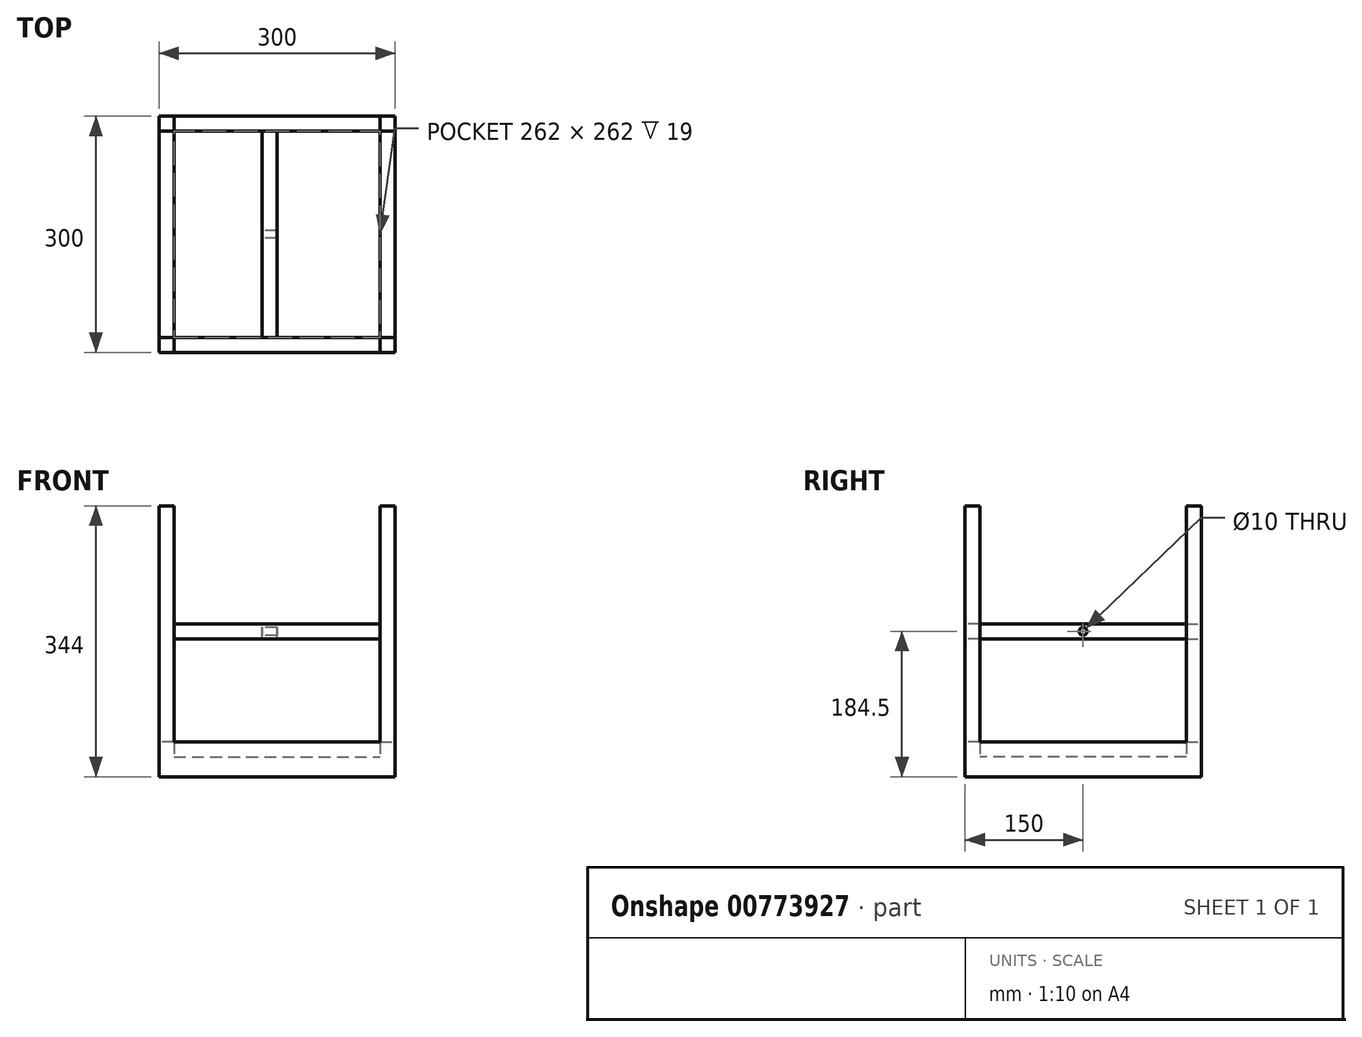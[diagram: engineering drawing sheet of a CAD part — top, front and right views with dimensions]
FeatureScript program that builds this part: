
annotation { "Feature Type Name" : "Feature", "Feature Type Description" : "" }
export const myFeature = defineFeature(function(context is Context, id is Id, definition is map)
    precondition{}
    {
        {
            var Q0;
            Q0=qCreatedBy(makeId("Top.planeOp"),FACE);
            var sketch = newSketch(context, id + "F0", { "sketchPlane" : qUnion([Q0])});
            skLineSegment(sketch, "E0.bottom", {"start": v(-150, -150) * mm, "end": v(150, -150) * mm});
            skLineSegment(sketch, "E0.top", {"start": v(-150, 150) * mm, "end": v(150, 150) * mm});
            skLineSegment(sketch, "E0.left", {"start": v(-150, -150) * mm, "end": v(-150, 150) * mm});
            skLineSegment(sketch, "E0.right", {"start": v(150, -150) * mm, "end": v(150, 150) * mm});
            skLineSegment(sketch, "E1.bottom", {"start": v(-131, 131) * mm, "end": v(131, 131) * mm});
            skLineSegment(sketch, "E1.top", {"start": v(-131, -131) * mm, "end": v(131, -131) * mm});
            skLineSegment(sketch, "E1.left", {"start": v(-131, 131) * mm, "end": v(-131, -131) * mm});
            skLineSegment(sketch, "E1.right", {"start": v(131, 131) * mm, "end": v(131, -131) * mm});
            skSolve(sketch);
        }
        {
            var Q0;
            Q0 = qSketchRegion(id + "F0", true);
            extrude(context, id + "F1", {"entities" : qUnion([Q0]), "depth" : 19 * mm, "offsetDistance" : 25 * mm});
        }
        {
            var Q0;
            Q0=makeQuery(id+"F1.opExtrude","CAP_FACE",FACE,{"disambiguationData":[OSD([sQuery(id+"F0.wireOp",EDGE,"E0.bottom"),sQuery(id+"F0.wireOp",EDGE,"E0.top"),sQuery(id+"F0.wireOp",EDGE,"E0.left"),sQuery(id+"F0.wireOp",EDGE,"E0.right"),sQuery(id+"F0.wireOp",EDGE,"E1.bottom"),sQuery(id+"F0.wireOp",EDGE,"E1.top"),sQuery(id+"F0.wireOp",EDGE,"E1.left"),sQuery(id+"F0.wireOp",EDGE,"E1.right")])],"isStart":true});
            var sketch = newSketch(context, id + "F2", { "sketchPlane" : qUnion([Q0])});
            skLineSegment(sketch, "E2.bottom", {"start": v(-131, -131) * mm, "end": v(131, -131) * mm});
            skLineSegment(sketch, "E2.top", {"start": v(-131, 131) * mm, "end": v(131, 131) * mm});
            skLineSegment(sketch, "E2.left", {"start": v(-131, -131) * mm, "end": v(-131, 131) * mm});
            skLineSegment(sketch, "E2.right", {"start": v(131, -131) * mm, "end": v(131, 131) * mm});
            skSolve(sketch);
        }
        {
            var Q0;
            Q0=makeQuery(id+"F2.imprint","IMPRINT",FACE,{"disambiguationData":[TD([[makeQuery(id+"F2.imprint","IMPRINT",EDGE,{"derivedFrom":sQuery(id+"F2.wireOp",EDGE,"E2.bottom")}),1.0]])]});
            var Q1;
            Q1=makeQuery(id+"F2.imprint","IMPRINT",FACE,{"disambiguationData":[TD([[makeQuery(id+"F2.imprint","IMPRINT",EDGE,{"derivedFrom":sQuery(id+"F2.wireOp",EDGE,"E2.bottom")}),-1.0]])]});
            extrude(context, id + "F3", {"entities" : qUnion([Q0, Q1]), "operationType" : NewBodyOperationType.ADD, "depth" : 25 * mm, "offsetDistance" : 25 * mm});
        }
        {
            var Q0;
            Q0=makeQuery(id+"F1.opExtrude","CAP_FACE",FACE,{"disambiguationData":[OSD([sQuery(id+"F0.wireOp",EDGE,"E0.bottom"),sQuery(id+"F0.wireOp",EDGE,"E0.top"),sQuery(id+"F0.wireOp",EDGE,"E0.left"),sQuery(id+"F0.wireOp",EDGE,"E0.right"),sQuery(id+"F0.wireOp",EDGE,"E1.bottom"),sQuery(id+"F0.wireOp",EDGE,"E1.top"),sQuery(id+"F0.wireOp",EDGE,"E1.left"),sQuery(id+"F0.wireOp",EDGE,"E1.right")])],"isStart":false});
            var sketch = newSketch(context, id + "F4", { "sketchPlane" : qUnion([Q0])});
            skLineSegment(sketch, "E3.bottom", {"start": v(131, 131) * mm, "end": v(150, 131) * mm});
            skLineSegment(sketch, "E3.top", {"start": v(131, 150) * mm, "end": v(150, 150) * mm});
            skLineSegment(sketch, "E3.left", {"start": v(131, 131) * mm, "end": v(131, 150) * mm});
            skLineSegment(sketch, "E3.right", {"start": v(150, 131) * mm, "end": v(150, 150) * mm});
            skLineSegment(sketch, "E4.bottom", {"start": v(-131, 131) * mm, "end": v(-150, 131) * mm});
            skLineSegment(sketch, "E4.top", {"start": v(-131, 150) * mm, "end": v(-150, 150) * mm});
            skLineSegment(sketch, "E4.left", {"start": v(-131, 131) * mm, "end": v(-131, 150) * mm});
            skLineSegment(sketch, "E4.right", {"start": v(-150, 131) * mm, "end": v(-150, 150) * mm});
            skLineSegment(sketch, "E5.bottom", {"start": v(131, -131) * mm, "end": v(150, -131) * mm});
            skLineSegment(sketch, "E5.top", {"start": v(131, -150) * mm, "end": v(150, -150) * mm});
            skLineSegment(sketch, "E5.left", {"start": v(131, -131) * mm, "end": v(131, -150) * mm});
            skLineSegment(sketch, "E5.right", {"start": v(150, -131) * mm, "end": v(150, -150) * mm});
            skLineSegment(sketch, "E6.bottom", {"start": v(-131, -131) * mm, "end": v(-150, -131) * mm});
            skLineSegment(sketch, "E6.top", {"start": v(-131, -150) * mm, "end": v(-150, -150) * mm});
            skLineSegment(sketch, "E6.left", {"start": v(-131, -131) * mm, "end": v(-131, -150) * mm});
            skLineSegment(sketch, "E6.right", {"start": v(-150, -131) * mm, "end": v(-150, -150) * mm});
            skSolve(sketch);
        }
        {
            var Q0;
            Q0 = qSketchRegion(id + "F4", true);
            extrude(context, id + "F5", {"entities" : qUnion([Q0]), "operationType" : NewBodyOperationType.ADD, "depth" : 300 * mm, "offsetDistance" : 25 * mm});
        }
        {
            var Q0;
            {var subQ0=sQuery(id+"F0.wireOp",EDGE,"E0.bottom");Q0=makeQuery(id+"F5.boolean.opBoolean","MERGE",FACE,{"derivedFrom":[makeQuery(id+"F3.boolean.opBoolean","MERGE",FACE,{"derivedFrom":[makeQuery(id+"F1.opExtrude","SWEPT_FACE",FACE,{"disambiguationData":[OSD([subQ0])]}),makeQuery(id+"F3.opExtrude","SWEPT_FACE",FACE,{"disambiguationData":[OSD([subQ0])]})]}),makeQuery(id+"F5.opExtrude","SWEPT_FACE",FACE,{"disambiguationData":[OSD([sQuery(id+"F4.wireOp",EDGE,"E5.top")])]}),makeQuery(id+"F5.opExtrude","SWEPT_FACE",FACE,{"disambiguationData":[OSD([sQuery(id+"F4.wireOp",EDGE,"E6.top")])]})]});}
            var sketch = newSketch(context, id + "F6", { "sketchPlane" : qUnion([Q0])});
            skLineSegment(sketch, "E7", {"start": v(-131, 169) * mm, "end": v(131, 169) * mm});
            skLineSegment(sketch, "E8", {"start": v(-131, 150) * mm, "end": v(131, 150) * mm});
            skSolve(sketch);
        }
        {
            var Q0;
            Q0 = qSketchRegion(id + "F6", true);
            var Q1;
            {var subQ0=sQuery(id+"F6.wireOp",EDGE,"E7");Q1=makeQuery(id+"F6.imprint","IMPRINT",FACE,{"disambiguationData":[TD([[makeQuery(id+"F6.imprint","IMPRINT",EDGE,{"derivedFrom":subQ0}),-1.0]])]});}
            extrude(context, id + "F7", {"entities" : qUnion([Q0, Q1]), "oppositeDirection" : true, "depth" : 19 * mm, "offsetDistance" : 25 * mm});
        }
        {
            var Q0;
            {var subQ0=sQuery(id+"F0.wireOp",EDGE,"E0.top");Q0=makeQuery(id+"F5.boolean.opBoolean","MERGE",FACE,{"derivedFrom":[makeQuery(id+"F3.boolean.opBoolean","MERGE",FACE,{"derivedFrom":[makeQuery(id+"F1.opExtrude","SWEPT_FACE",FACE,{"disambiguationData":[OSD([subQ0])]}),makeQuery(id+"F3.opExtrude","SWEPT_FACE",FACE,{"disambiguationData":[OSD([subQ0])]})]}),makeQuery(id+"F5.opExtrude","SWEPT_FACE",FACE,{"disambiguationData":[OSD([sQuery(id+"F4.wireOp",EDGE,"E3.top")])]}),makeQuery(id+"F5.opExtrude","SWEPT_FACE",FACE,{"disambiguationData":[OSD([sQuery(id+"F4.wireOp",EDGE,"E4.top")])]})]});}
            var sketch = newSketch(context, id + "F8", { "sketchPlane" : qUnion([Q0])});
            skLineSegment(sketch, "E9", {"start": v(-131, 169) * mm, "end": v(131, 169) * mm});
            skLineSegment(sketch, "E10", {"start": v(-131, 150) * mm, "end": v(131, 150) * mm});
            skSolve(sketch);
        }
        {
            var Q0;
            Q0 = qSketchRegion(id + "F8", true);
            var Q1;
            {var subQ0=sQuery(id+"F8.wireOp",EDGE,"E9");Q1=makeQuery(id+"F8.imprint","IMPRINT",FACE,{"disambiguationData":[TD([[makeQuery(id+"F8.imprint","IMPRINT",EDGE,{"derivedFrom":subQ0}),-1.0]])]});}
            extrude(context, id + "F9", {"entities" : qUnion([Q0, Q1]), "oppositeDirection" : true, "depth" : 19 * mm, "offsetDistance" : 25 * mm});
        }
        {
            var Q0;
            Q0=makeQuery(id+"F9.opExtrude","CAP_FACE",FACE,{"disambiguationData":[OSD([sQuery(id+"F0.wireOp",EDGE,"E0.top"),sQuery(id+"F4.wireOp",EDGE,"E3.top"),sQuery(id+"F4.wireOp",EDGE,"E3.left"),sQuery(id+"F4.wireOp",EDGE,"E4.top"),sQuery(id+"F4.wireOp",EDGE,"E4.left"),sQuery(id+"F8.wireOp",EDGE,"E9"),sQuery(id+"F8.wireOp",EDGE,"E10")])],"isStart":false});
            var sketch = newSketch(context, id + "F10", { "sketchPlane" : qUnion([Q0])});
            skLineSegment(sketch, "E11", {"start": v(0, 150) * mm, "end": v(0, 169) * mm});
            skLineSegment(sketch, "E12", {"start": v(-19, 150) * mm, "end": v(-19, 169) * mm});
            skSolve(sketch);
        }
        {
            var Q0;
            {var subQ0=sQuery(id+"F10.wireOp",EDGE,"E11");Q0=makeQuery(id+"F10.imprint","IMPRINT",FACE,{"disambiguationData":[TD([[makeQuery(id+"F10.imprint","IMPRINT",EDGE,{"derivedFrom":subQ0}),1.0]])]});}
            extrude(context, id + "F11", {"entities" : qUnion([Q0]), "depth" : 262 * mm, "offsetDistance" : 25 * mm});
        }
        {
            var Q0;
            Q0=makeQuery(id+"F11.opExtrude","SWEPT_FACE",FACE,{"disambiguationData":[OSD([sQuery(id+"F10.wireOp",EDGE,"E12")])]});
            var sketch = newSketch(context, id + "F12", { "sketchPlane" : qUnion([Q0])});
            skCircle(sketch, "E13", {"center": v(0, 159.5) * mm, "radius": 5 * mm});
            skSolve(sketch);
        }
        {
            var Q0;
            Q0 = qSketchRegion(id + "F12", true);
            extrude(context, id + "F13", {"entities" : qUnion([Q0]), "operationType" : NewBodyOperationType.REMOVE, "oppositeDirection" : true, "depth" : 25 * mm, "offsetDistance" : 25 * mm});
        }
    });
